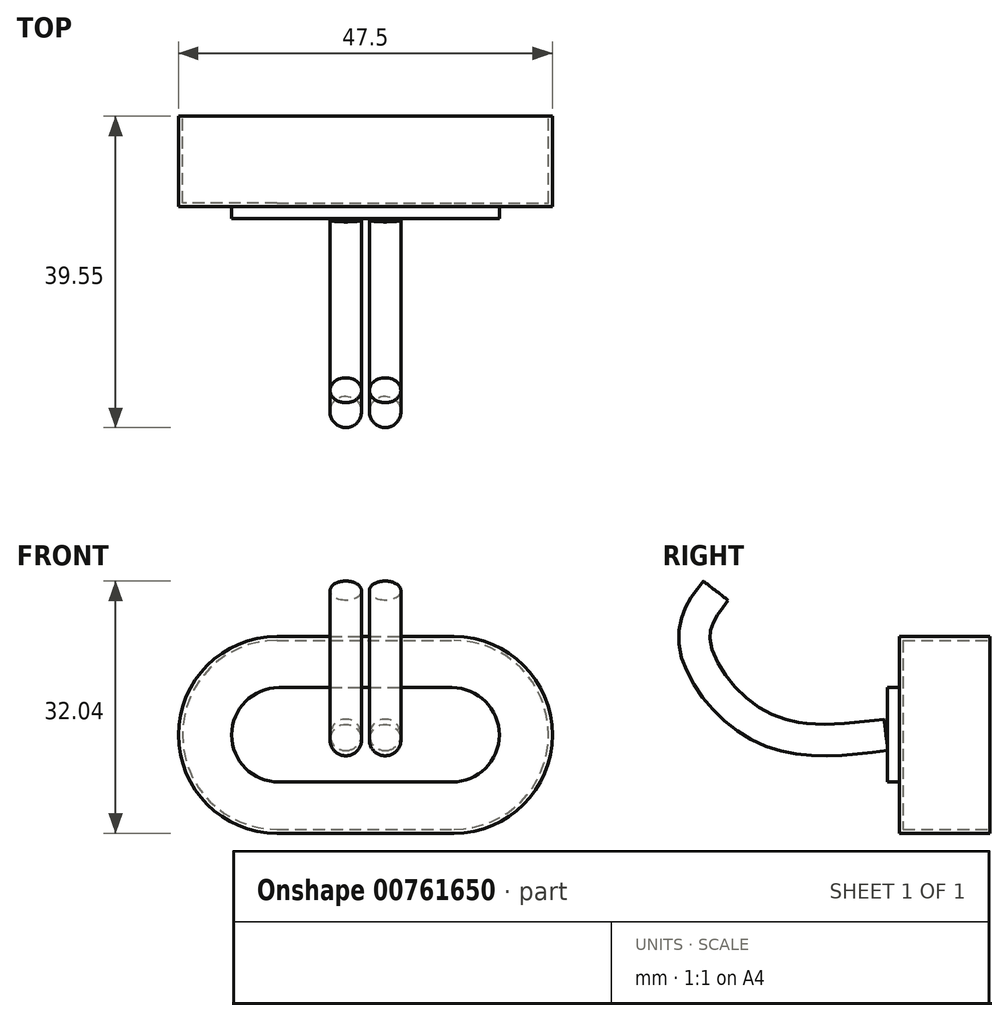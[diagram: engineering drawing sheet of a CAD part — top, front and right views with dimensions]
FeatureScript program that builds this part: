
annotation { "Feature Type Name" : "Feature", "Feature Type Description" : "" }
export const myFeature = defineFeature(function(context is Context, id is Id, definition is map)
    precondition{}
    {
        {
            var Q0;
            Q0=qCreatedBy(makeId("Front.planeOp"),FACE);
            var sketch = newSketch(context, id + "F0", { "sketchPlane" : qUnion([Q0])});
            skLineSegment(sketch, "E0.bottom", {"start": v(-11.25, 12.5) * mm, "end": v(11.25, 12.5) * mm});
            skLineSegment(sketch, "E0.top", {"start": v(-11.25, -12.5) * mm, "end": v(11.25, -12.5) * mm});
            skLineSegment(sketch, "E0.left", {"start": v(-23.75, 0) * mm, "end": v(-23.75, 0) * mm});
            skLineSegment(sketch, "E0.right", {"start": v(23.75, 0) * mm, "end": v(23.75, 0) * mm});
            skPoint(sketch, "E0.middle", {"position": v(0, 0) * mm});
            skPoint(sketch, "E1.visualSharp", {"position": v(-23.75, 12.5) * mm});
            skArc(sketch, "E1.filletArc", {"start": v(-11.25, 12.5) * mm, "mid": v(-20.09, 8.84) * mm, "end": v(-23.75, 0) * mm});
            skPoint(sketch, "E2.visualSharp", {"position": v(-23.75, -12.5) * mm});
            skArc(sketch, "E2.filletArc", {"start": v(-23.75, 0) * mm, "mid": v(-20.09, -8.84) * mm, "end": v(-11.25, -12.5) * mm});
            skPoint(sketch, "E3.visualSharp", {"position": v(23.75, -12.5) * mm});
            skArc(sketch, "E3.filletArc", {"start": v(11.25, -12.5) * mm, "mid": v(20.09, -8.84) * mm, "end": v(23.75, 0) * mm});
            skPoint(sketch, "E4.visualSharp", {"position": v(23.75, 12.5) * mm});
            skArc(sketch, "E4.filletArc", {"start": v(23.75, 0) * mm, "mid": v(20.09, 8.84) * mm, "end": v(11.25, 12.5) * mm});
            skSolve(sketch);
        }
        {
            var Q0;
            Q0 = qSketchRegion(id + "F0", true);
            extrude(context, id + "F1", {"entities" : qUnion([Q0]), "depth" : 11.5 * mm, "offsetDistance" : 25 * mm});
        }
        {
            var Q0;
            Q0=makeQuery(id+"F1.opExtrude","CAP_FACE",FACE,{"disambiguationData":[OSD([sQuery(id+"F0.wireOp",EDGE,"E0.bottom"),sQuery(id+"F0.wireOp",EDGE,"E0.top"),sQuery(id+"F0.wireOp",EDGE,"E1.filletArc"),sQuery(id+"F0.wireOp",EDGE,"E2.filletArc"),sQuery(id+"F0.wireOp",EDGE,"E3.filletArc"),sQuery(id+"F0.wireOp",EDGE,"E4.filletArc")])],"isStart":true});
            shell(context, id + "F2", {"entities" : qUnion([Q0]), "thickness" : 0.5 * mm});
        }
        {
            var Q0;
            Q0=makeQuery(id+"F1.opExtrude","CAP_FACE",FACE,{"disambiguationData":[OSD([sQuery(id+"F0.wireOp",EDGE,"E0.bottom"),sQuery(id+"F0.wireOp",EDGE,"E0.top"),sQuery(id+"F0.wireOp",EDGE,"E1.filletArc"),sQuery(id+"F0.wireOp",EDGE,"E2.filletArc"),sQuery(id+"F0.wireOp",EDGE,"E3.filletArc"),sQuery(id+"F0.wireOp",EDGE,"E4.filletArc")])],"isStart":false});
            var sketch = newSketch(context, id + "F3", { "sketchPlane" : qUnion([Q0])});
            skLineSegment(sketch, "E5.bottom", {"start": v(-11, -6) * mm, "end": v(11, -6) * mm});
            skLineSegment(sketch, "E5.top", {"start": v(-11, 6) * mm, "end": v(11, 6) * mm});
            skLineSegment(sketch, "E5.left", {"start": v(-17, 0) * mm, "end": v(-17, 0) * mm});
            skLineSegment(sketch, "E5.right", {"start": v(17, 0) * mm, "end": v(17, 0) * mm});
            skPoint(sketch, "E5.middle", {"position": v(0, 0) * mm});
            skPoint(sketch, "E6.visualSharp", {"position": v(-17, 6) * mm});
            skArc(sketch, "E6.filletArc", {"start": v(-11, 6) * mm, "mid": v(-15.24, 4.24) * mm, "end": v(-17, 0) * mm});
            skPoint(sketch, "E7.visualSharp", {"position": v(-17, -6) * mm});
            skArc(sketch, "E7.filletArc", {"start": v(-17, 0) * mm, "mid": v(-15.24, -4.24) * mm, "end": v(-11, -6) * mm});
            skPoint(sketch, "E8.visualSharp", {"position": v(17, -6) * mm});
            skArc(sketch, "E8.filletArc", {"start": v(11, -6) * mm, "mid": v(15.24, -4.24) * mm, "end": v(17, 0) * mm});
            skPoint(sketch, "E9.visualSharp", {"position": v(17, 6) * mm});
            skArc(sketch, "E9.filletArc", {"start": v(17, 0) * mm, "mid": v(15.24, 4.24) * mm, "end": v(11, 6) * mm});
            skSolve(sketch);
        }
        {
            var Q0;
            Q0=makeQuery(id+"F3.imprint","IMPRINT",FACE,{"disambiguationData":[TD([[makeQuery(id+"F3.imprint","IMPRINT",EDGE,{"derivedFrom":sQuery(id+"F3.wireOp",EDGE,"E5.bottom")}),1.0]])]});
            extrude(context, id + "F4", {"entities" : qUnion([Q0]), "operationType" : NewBodyOperationType.ADD, "depth" : 1.5 * mm, "offsetDistance" : 25 * mm});
        }
        {
            var Q0;
            Q0=qCreatedBy(makeId("Right.planeOp"),FACE);
            var sketch = newSketch(context, id + "F5", { "sketchPlane" : qUnion([Q0])});
            skFitSpline(sketch, "E10", {"points": [v(-13.17, 0) * mm, v(-29.18, 1.07) * mm, v(-37.53, 11.95) * mm, v(-34.8, 18.31) * mm], "startDerivative": vector(-43.57, -5.39) * mm, "endDerivative": vector(17.33, 22.35) * mm});
            skSolve(sketch);
        }
        {
            var Q0;
            Q0=sQuery(id+"F5.wireOp",VERTEX,"E10.end");
            var Q1;
            Q1=sQuery(id+"F5.wireOp",EDGE,"E10");
            cPlane(context, id + "F6", {"entities" : qUnion([Q0, Q1]), "cplaneType" : CPlaneType.CURVE_POINT, "offset" : 25 * mm, "width" : 150 * mm, "height" : 150 * mm});
        }
        {
            var Q0;
            Q0=qCreatedBy(id+"F6.planeOp",FACE);
            var sketch = newSketch(context, id + "F7", { "sketchPlane" : qUnion([Q0])});
            skPoint(sketch, "E11", {"position": v(0, -38.73) * mm});
            skLineSegment(sketch, "E12", {"start": v(0, -38.73) * mm, "end": v(-2.5, -38.73) * mm, "construction": true});
            skCircle(sketch, "E13", {"center": v(-2.5, -38.73) * mm, "radius": 2 * mm});
            skCircle(sketch, "E14.1.0.0", {"center": v(2.5, -38.73) * mm, "radius": 2 * mm});
            skLineSegment(sketch, "E14.direction1", {"start": v(-2.5, -38.73) * mm, "end": v(2.5, -38.73) * mm, "construction": true});
            skSolve(sketch);
        }
        {
            var Q0;
            Q0=makeQuery(id+"F7.imprint","IMPRINT",FACE,{"disambiguationData":[TD([[makeQuery(id+"F7.imprint","IMPRINT",EDGE,{"derivedFrom":sQuery(id+"F7.wireOp",EDGE,"E13")}),1.0]])]});
            var Q1;
            Q1=sQuery(id+"F5.wireOp",EDGE,"E10");
            sweep(context, id + "F8", {"profiles" : qUnion([Q0]), "path" : qUnion([Q1])});
        }
        {
            var Q0;
            Q0=makeQuery(id+"F7.imprint","IMPRINT",FACE,{"disambiguationData":[TD([[makeQuery(id+"F7.imprint","IMPRINT",EDGE,{"derivedFrom":sQuery(id+"F7.wireOp",EDGE,"E14.1.0.0")}),1.0]])]});
            var Q1;
            Q1=sQuery(id+"F5.wireOp",EDGE,"E10");
            sweep(context, id + "F9", {"profiles" : qUnion([Q0]), "path" : qUnion([Q1])});
        }
    });
